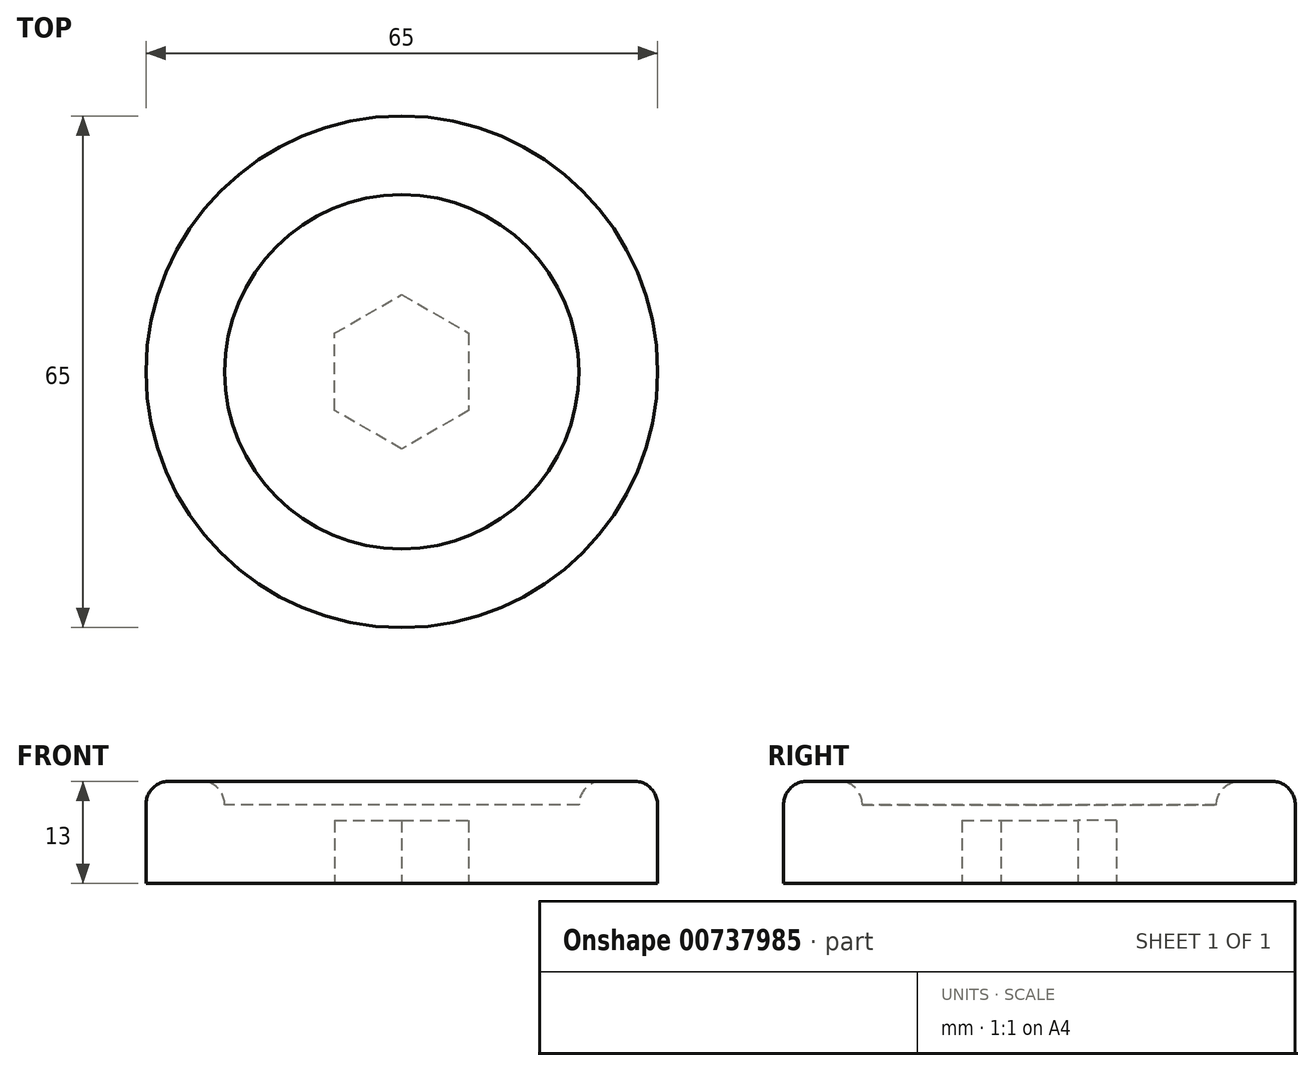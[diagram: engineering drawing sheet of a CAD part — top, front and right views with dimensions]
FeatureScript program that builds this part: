
annotation { "Feature Type Name" : "Feature", "Feature Type Description" : "" }
export const myFeature = defineFeature(function(context is Context, id is Id, definition is map)
    precondition{}
    {
        {
            var Q0;
            Q0=qCreatedBy(makeId("Top.planeOp"),FACE);
            var sketch = newSketch(context, id + "F0", { "sketchPlane" : qUnion([Q0])});
            skCircle(sketch, "E0.cCircle", {"center": v(0, 0) * mm, "radius": 9.81 * mm, "construction": true});
            skLineSegment(sketch, "E0.0", {"start": v(0, 9.81) * mm, "end": v(8.5, 4.9) * mm});
            skLineSegment(sketch, "E0.1", {"start": v(8.5, 4.9) * mm, "end": v(8.5, -4.9) * mm});
            skLineSegment(sketch, "E0.2", {"start": v(8.5, -4.9) * mm, "end": v(0, -9.81) * mm});
            skLineSegment(sketch, "E0.3", {"start": v(0, -9.81) * mm, "end": v(-8.5, -4.9) * mm});
            skLineSegment(sketch, "E0.4", {"start": v(-8.5, -4.9) * mm, "end": v(-8.5, 4.9) * mm});
            skLineSegment(sketch, "E0.5", {"start": v(-8.5, 4.9) * mm, "end": v(0, 9.81) * mm});
            skCircle(sketch, "E1", {"center": v(0, 0) * mm, "radius": 32.5 * mm});
            skCircle(sketch, "E2", {"center": v(0, 0) * mm, "radius": 22.5 * mm});
            skSolve(sketch);
        }
        {
            var Q0;
            Q0=makeQuery(id+"F0.imprint","IMPRINT",FACE,{"disambiguationData":[TD([[makeQuery(id+"F0.imprint","IMPRINT",EDGE,{"derivedFrom":sQuery(id+"F0.wireOp",EDGE,"E1")}),1.0]])]});
            var Q1;
            Q1=makeQuery(id+"F0.imprint","IMPRINT",FACE,{"disambiguationData":[TD([[makeQuery(id+"F0.imprint","IMPRINT",EDGE,{"derivedFrom":sQuery(id+"F0.wireOp",EDGE,"E0.0")}),1.0]])]});
            var Q2;
            Q2=makeQuery(id+"F0.imprint","IMPRINT",FACE,{"disambiguationData":[TD([[makeQuery(id+"F0.imprint","IMPRINT",EDGE,{"derivedFrom":sQuery(id+"F0.wireOp",EDGE,"E0.0")}),-1.0]])]});
            extrude(context, id + "F1", {"entities" : qUnion([Q0, Q1, Q2]), "depth" : 10 * mm, "offsetDistance" : 25 * mm});
        }
        {
            var Q0;
            Q0=makeQuery(id+"F0.imprint","IMPRINT",FACE,{"disambiguationData":[TD([[makeQuery(id+"F0.imprint","IMPRINT",EDGE,{"derivedFrom":sQuery(id+"F0.wireOp",EDGE,"E1")}),1.0]])]});
            extrude(context, id + "F2", {"entities" : qUnion([Q0]), "operationType" : NewBodyOperationType.ADD, "depth" : 13 * mm, "offsetDistance" : 25 * mm});
        }
        {
            var Q0;
            Q0=makeQuery(id+"F0.imprint","IMPRINT",FACE,{"disambiguationData":[TD([[makeQuery(id+"F0.imprint","IMPRINT",EDGE,{"derivedFrom":sQuery(id+"F0.wireOp",EDGE,"E0.0")}),-1.0]])]});
            extrude(context, id + "F3", {"entities" : qUnion([Q0]), "operationType" : NewBodyOperationType.REMOVE, "depth" : 8 * mm, "offsetDistance" : 25 * mm});
        }
        {
            var Q0;
            Q0=makeQuery(id+"F2.opExtrude","CAP_EDGE",EDGE,{"disambiguationData":[OSD([sQuery(id+"F0.wireOp",EDGE,"E1")])],"isStart":false});
            var Q1;
            Q1=makeQuery(id+"F2.opExtrude","CAP_EDGE",EDGE,{"disambiguationData":[OSD([sQuery(id+"F0.wireOp",EDGE,"E2")])],"isStart":false});
            fillet(context, id + "F4", {"entities" : qUnion([Q0, Q1]), "radius" : 3 * mm, "tangentPropagation" : true, "allowEdgeOverflow" : false});
        }
    });
